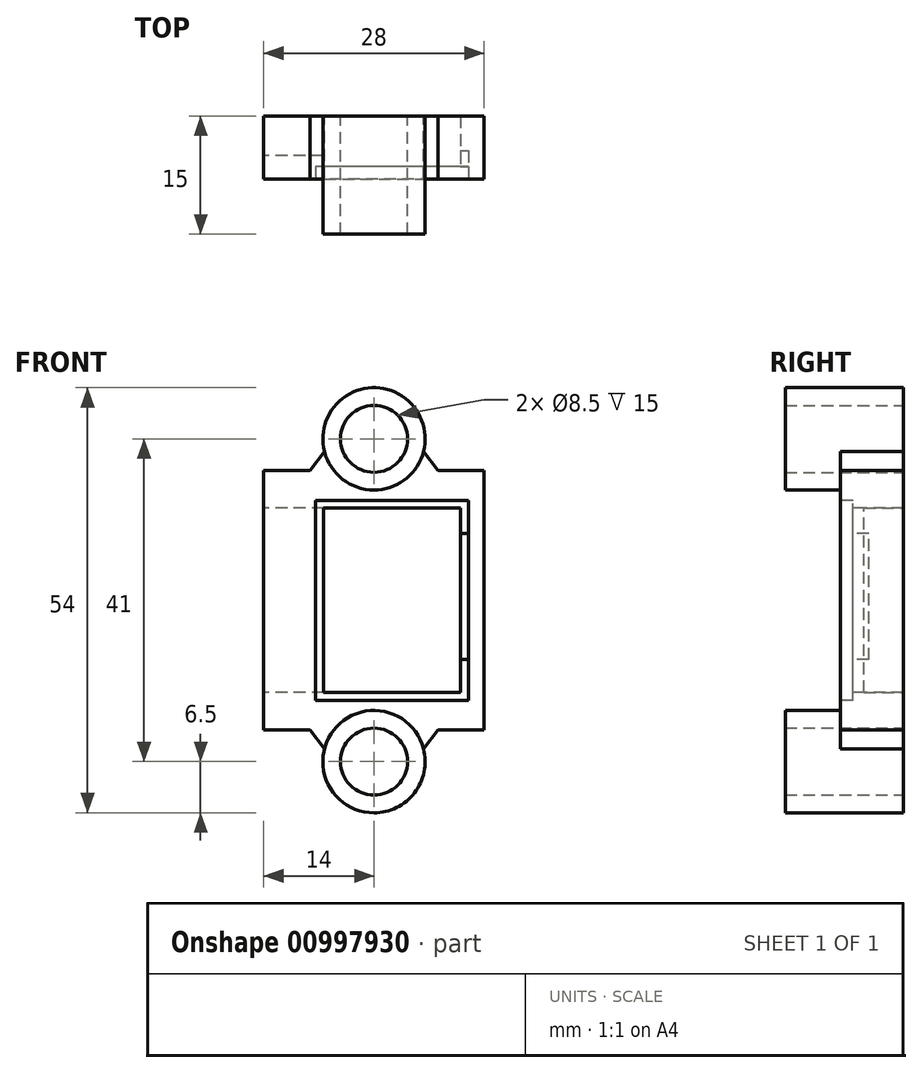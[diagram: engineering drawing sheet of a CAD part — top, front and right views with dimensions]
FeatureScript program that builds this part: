
annotation { "Feature Type Name" : "Feature", "Feature Type Description" : "" }
export const myFeature = defineFeature(function(context is Context, id is Id, definition is map)
    precondition{}
    {
        {
            var Q0;
            Q0=qCreatedBy(makeId("Front.planeOp"),FACE);
            var sketch = newSketch(context, id + "F0", { "sketchPlane" : qUnion([Q0])});
            skLineSegment(sketch, "E0.bottom", {"start": v(14, -16.5) * mm, "end": v(-14, -16.5) * mm});
            skLineSegment(sketch, "E0.top", {"start": v(14, 16.5) * mm, "end": v(-14, 16.5) * mm});
            skLineSegment(sketch, "E0.left", {"start": v(14, -16.5) * mm, "end": v(14, 16.5) * mm});
            skLineSegment(sketch, "E0.right", {"start": v(-14, -16.5) * mm, "end": v(-14, 16.5) * mm});
            skPoint(sketch, "E0.middle", {"position": v(0, 0) * mm});
            skCircle(sketch, "E1", {"center": v(0, 20.5) * mm, "radius": 6.5 * mm});
            skCircle(sketch, "E2", {"center": v(0, -20.5) * mm, "radius": 6.5 * mm});
            skCircle(sketch, "E3", {"center": v(0, 20.5) * mm, "radius": 4.25 * mm});
            skCircle(sketch, "E4", {"center": v(0, -20.5) * mm, "radius": 4.25 * mm});
            skSolve(sketch);
        }
        {
            var Q0;
            {var subQ7=sQuery(id+"F0.wireOp",EDGE,"E0.left");Q0=makeQuery(id+"F0.imprint","IMPRINT",FACE,{"disambiguationData":[TD([[makeQuery(id+"F0.imprint","IMPRINT",EDGE,{"derivedFrom":subQ7}),1.0]])]});}
            extrude(context, id + "F1", {"entities" : qUnion([Q0]), "depth" : 8 * mm, "offsetDistance" : 25 * mm});
        }
        {
            var Q0;
            {var subQ0=sQuery(id+"F0.wireOp",EDGE,"E1");var subQ1=sQuery(id+"F0.wireOp",EDGE,"E0.top");var subQ2=makeQuery(id+"F0.imprint","INTERSECT",VERTEX,{"disambiguationData":[OD(0.0)],"derivedFrom":[subQ1,subQ0]});Q0=makeQuery(id+"F0.imprint","IMPRINT",FACE,{"disambiguationData":[TD([[makeQuery(id+"F0.imprint","IMPRINT",EDGE,{"disambiguationData":[TD([[subQ2,-1.0]])],"derivedFrom":subQ1}),-1.0]])]});}
            var Q1;
            {var subQ0=sQuery(id+"F0.wireOp",EDGE,"E1");var subQ1=sQuery(id+"F0.wireOp",EDGE,"E0.top");var subQ2=makeQuery(id+"F0.imprint","INTERSECT",VERTEX,{"disambiguationData":[OD(0.0)],"derivedFrom":[subQ1,subQ0]});Q1=makeQuery(id+"F0.imprint","IMPRINT",FACE,{"disambiguationData":[TD([[makeQuery(id+"F0.imprint","IMPRINT",EDGE,{"disambiguationData":[TD([[subQ2,-1.0]])],"derivedFrom":subQ1}),1.0]])]});}
            var Q2;
            {var subQ0=sQuery(id+"F0.wireOp",EDGE,"E2");var subQ1=sQuery(id+"F0.wireOp",EDGE,"E0.bottom");var subQ2=makeQuery(id+"F0.imprint","INTERSECT",VERTEX,{"disambiguationData":[OD(0.0)],"derivedFrom":[subQ1,subQ0]});Q2=makeQuery(id+"F0.imprint","IMPRINT",FACE,{"disambiguationData":[TD([[makeQuery(id+"F0.imprint","IMPRINT",EDGE,{"disambiguationData":[TD([[subQ2,-1.0]])],"derivedFrom":subQ1}),-1.0]])]});}
            var Q3;
            {var subQ0=sQuery(id+"F0.wireOp",EDGE,"E2");var subQ1=sQuery(id+"F0.wireOp",EDGE,"E0.bottom");var subQ2=makeQuery(id+"F0.imprint","INTERSECT",VERTEX,{"disambiguationData":[OD(0.0)],"derivedFrom":[subQ1,subQ0]});Q3=makeQuery(id+"F0.imprint","IMPRINT",FACE,{"disambiguationData":[TD([[makeQuery(id+"F0.imprint","IMPRINT",EDGE,{"disambiguationData":[TD([[subQ2,-1.0]])],"derivedFrom":subQ1}),1.0]])]});}
            extrude(context, id + "F2", {"entities" : qUnion([Q0, Q1, Q2, Q3]), "depth" : 14 * mm, "offsetDistance" : 25 * mm});
        }
        {
            var Q0;
            {var subQ0=sQuery(id+"F0.wireOp",EDGE,"E2");var subQ1=sQuery(id+"F0.wireOp",EDGE,"E0.bottom");var subQ2=makeQuery(id+"F0.imprint","INTERSECT",VERTEX,{"disambiguationData":[OD(0.0)],"derivedFrom":[subQ1,subQ0]});Q0=makeQuery(id+"F0.imprint","IMPRINT",FACE,{"disambiguationData":[TD([[makeQuery(id+"F0.imprint","IMPRINT",EDGE,{"disambiguationData":[TD([[subQ2,-1.0]])],"derivedFrom":subQ1}),1.0]])]});}
            var Q1;
            {var subQ0=sQuery(id+"F0.wireOp",EDGE,"E2");var subQ1=sQuery(id+"F0.wireOp",EDGE,"E0.bottom");var subQ2=makeQuery(id+"F0.imprint","INTERSECT",VERTEX,{"disambiguationData":[OD(0.0)],"derivedFrom":[subQ1,subQ0]});Q1=makeQuery(id+"F0.imprint","IMPRINT",FACE,{"disambiguationData":[TD([[makeQuery(id+"F0.imprint","IMPRINT",EDGE,{"disambiguationData":[TD([[subQ2,-1.0]])],"derivedFrom":subQ1}),-1.0]])]});}
            var Q2;
            {var subQ0=sQuery(id+"F0.wireOp",EDGE,"E1");var subQ1=sQuery(id+"F0.wireOp",EDGE,"E0.top");var subQ2=makeQuery(id+"F0.imprint","INTERSECT",VERTEX,{"disambiguationData":[OD(0.0)],"derivedFrom":[subQ1,subQ0]});Q2=makeQuery(id+"F0.imprint","IMPRINT",FACE,{"disambiguationData":[TD([[makeQuery(id+"F0.imprint","IMPRINT",EDGE,{"disambiguationData":[TD([[subQ2,-1.0]])],"derivedFrom":subQ1}),1.0]])]});}
            var Q3;
            {var subQ0=sQuery(id+"F0.wireOp",EDGE,"E1");var subQ1=sQuery(id+"F0.wireOp",EDGE,"E0.top");var subQ2=makeQuery(id+"F0.imprint","INTERSECT",VERTEX,{"disambiguationData":[OD(0.0)],"derivedFrom":[subQ1,subQ0]});Q3=makeQuery(id+"F0.imprint","IMPRINT",FACE,{"disambiguationData":[TD([[makeQuery(id+"F0.imprint","IMPRINT",EDGE,{"disambiguationData":[TD([[subQ2,-1.0]])],"derivedFrom":subQ1}),-1.0]])]});}
            extrude(context, id + "F3", {"entities" : qUnion([Q0, Q1, Q2, Q3]), "operationType" : NewBodyOperationType.ADD, "depth" : 15 * mm, "offsetDistance" : 25 * mm});
        }
        {
            var Q0;
            {var subQ0=sQuery(id+"F0.wireOp",EDGE,"E1");var subQ1=sQuery(id+"F0.wireOp",EDGE,"E0.top");Q0=makeQuery(id+"F1.opExtrude","SWEPT_EDGE",EDGE,{"disambiguationData":[OSD([subQ1,subQ0]),TDD([makeQuery(id+"F0.imprint","INTERSECT",VERTEX,{"disambiguationData":[OD(1.0)],"derivedFrom":[subQ1,subQ0]})])]});}
            var Q1;
            {var subQ0=sQuery(id+"F0.wireOp",EDGE,"E1");var subQ1=sQuery(id+"F0.wireOp",EDGE,"E0.top");Q1=makeQuery(id+"F1.opExtrude","SWEPT_EDGE",EDGE,{"disambiguationData":[OSD([subQ1,subQ0]),TDD([makeQuery(id+"F0.imprint","INTERSECT",VERTEX,{"disambiguationData":[OD(0.0)],"derivedFrom":[subQ1,subQ0]})])]});}
            var Q2;
            {var subQ0=sQuery(id+"F0.wireOp",EDGE,"E2");var subQ1=sQuery(id+"F0.wireOp",EDGE,"E0.bottom");Q2=makeQuery(id+"F1.opExtrude","SWEPT_EDGE",EDGE,{"disambiguationData":[OSD([subQ1,subQ0]),TDD([makeQuery(id+"F0.imprint","INTERSECT",VERTEX,{"disambiguationData":[OD(0.0)],"derivedFrom":[subQ1,subQ0]})])]});}
            var Q3;
            {var subQ0=sQuery(id+"F0.wireOp",EDGE,"E2");var subQ1=sQuery(id+"F0.wireOp",EDGE,"E0.bottom");Q3=makeQuery(id+"F1.opExtrude","SWEPT_EDGE",EDGE,{"disambiguationData":[OSD([subQ1,subQ0]),TDD([makeQuery(id+"F0.imprint","INTERSECT",VERTEX,{"disambiguationData":[OD(1.0)],"derivedFrom":[subQ1,subQ0]})])]});}
            chamfer(context, id + "F4", {"entities" : qUnion([Q0, Q1, Q2, Q3]), "width" : 1.9 * mm, "tangentPropagation" : true});
        }
        {
            var Q0;
            Q0=makeQuery(id+"F1.opExtrude","CAP_FACE",FACE,{"disambiguationData":[OSD([sQuery(id+"F0.wireOp",EDGE,"E0.bottom"),sQuery(id+"F0.wireOp",EDGE,"E0.top"),sQuery(id+"F0.wireOp",EDGE,"E0.left"),sQuery(id+"F0.wireOp",EDGE,"E0.right"),sQuery(id+"F0.wireOp",EDGE,"E1"),sQuery(id+"F0.wireOp",EDGE,"E2")])],"isStart":false});
            var sketch = newSketch(context, id + "F5", { "sketchPlane" : qUnion([Q0])});
            skLineSegment(sketch, "E5.bottom", {"start": v(12, -12.7) * mm, "end": v(-7.4, -12.7) * mm});
            skLineSegment(sketch, "E5.top", {"start": v(12, 12.7) * mm, "end": v(-7.4, 12.7) * mm});
            skLineSegment(sketch, "E5.left", {"start": v(12, -12.7) * mm, "end": v(12, 12.7) * mm});
            skLineSegment(sketch, "E5.right", {"start": v(-7.4, -12.7) * mm, "end": v(-7.4, 12.7) * mm});
            skPoint(sketch, "E5.middle", {"position": v(2.3, 0) * mm});
            skSolve(sketch);
        }
        {
            var Q0;
            Q0 = qSketchRegion(id + "F5", true);
            extrude(context, id + "F6", {"entities" : qUnion([Q0]), "operationType" : NewBodyOperationType.REMOVE, "oppositeDirection" : true, "depth" : 1.6 * mm, "offsetDistance" : 25 * mm});
        }
        {
            var Q0;
            Q0=makeQuery(id+"F6.boolean.opBoolean","COPY",FACE,{"derivedFrom":makeQuery(id+"F6.opExtrude","CAP_FACE",FACE,{"disambiguationData":[OSD([sQuery(id+"F5.wireOp",EDGE,"E5.bottom"),sQuery(id+"F5.wireOp",EDGE,"E5.top"),sQuery(id+"F5.wireOp",EDGE,"E5.left"),sQuery(id+"F5.wireOp",EDGE,"E5.right")])],"isStart":false})});
            var sketch = newSketch(context, id + "F7", { "sketchPlane" : qUnion([Q0])});
            skLineSegment(sketch, "E6.bottom", {"start": v(11, -11.7) * mm, "end": v(-6.4, -11.7) * mm});
            skLineSegment(sketch, "E6.top", {"start": v(11, 11.7) * mm, "end": v(-6.4, 11.7) * mm});
            skLineSegment(sketch, "E6.left", {"start": v(11, -11.7) * mm, "end": v(11, 11.7) * mm});
            skLineSegment(sketch, "E6.right", {"start": v(-6.4, -11.7) * mm, "end": v(-6.4, 11.7) * mm});
            skPoint(sketch, "E6.middle", {"position": v(2.3, 0) * mm});
            skSolve(sketch);
        }
        {
            var Q0;
            Q0=makeQuery(id+"F7.imprint","IMPRINT",FACE,{"disambiguationData":[TD([[makeQuery(id+"F7.imprint","IMPRINT",EDGE,{"derivedFrom":sQuery(id+"F7.wireOp",EDGE,"E6.bottom")}),-1.0]])]});
            extrude(context, id + "F8", {"entities" : qUnion([Q0]), "operationType" : NewBodyOperationType.REMOVE, "oppositeDirection" : true, "depth" : 25 * mm, "offsetDistance" : 25 * mm});
        }
        {
            var Q0;
            {var subQ7=sQuery(id+"F0.wireOp",EDGE,"E0.left");Q0=makeQuery(id+"F0.imprint","IMPRINT",FACE,{"disambiguationData":[TD([[makeQuery(id+"F0.imprint","IMPRINT",EDGE,{"derivedFrom":subQ7}),1.0]])]});}
            var sketch = newSketch(context, id + "F9", { "sketchPlane" : qUnion([Q0])});
            skLineSegment(sketch, "E7.bottom", {"start": v(3.7, -11.7) * mm, "end": v(-16.31, -11.7) * mm});
            skLineSegment(sketch, "E7.top", {"start": v(3.7, 11.7) * mm, "end": v(-16.31, 11.7) * mm});
            skLineSegment(sketch, "E7.left", {"start": v(3.7, -11.7) * mm, "end": v(3.7, 11.7) * mm});
            skLineSegment(sketch, "E7.right", {"start": v(-16.31, -11.7) * mm, "end": v(-16.31, 11.7) * mm});
            skPoint(sketch, "E7.middle", {"position": v(-6.3, 0) * mm});
            skSolve(sketch);
        }
        {
            var Q0;
            {var subQ0=sQuery(id+"F9.wireOp",EDGE,"E7.left");Q0=makeQuery(id+"F9.imprint","IMPRINT",FACE,{"disambiguationData":[TD([[makeQuery(id+"F9.imprint","IMPRINT",EDGE,{"derivedFrom":subQ0}),1.0]])]});}
            extrude(context, id + "F10", {"entities" : qUnion([Q0]), "operationType" : NewBodyOperationType.REMOVE, "depth" : 5 * mm, "offsetDistance" : 25 * mm});
        }
        {
            var Q0;
            Q0=makeQuery(id+"F6.boolean.opBoolean","COPY",FACE,{"derivedFrom":makeQuery(id+"F6.opExtrude","CAP_FACE",FACE,{"disambiguationData":[OSD([sQuery(id+"F5.wireOp",EDGE,"E5.bottom"),sQuery(id+"F5.wireOp",EDGE,"E5.top"),sQuery(id+"F5.wireOp",EDGE,"E5.left"),sQuery(id+"F5.wireOp",EDGE,"E5.right")])],"isStart":false})});
            var sketch = newSketch(context, id + "F11", { "sketchPlane" : qUnion([Q0])});
            skLineSegment(sketch, "E8.bottom", {"start": v(10, -7.53) * mm, "end": v(12, -7.53) * mm});
            skLineSegment(sketch, "E8.top", {"start": v(10, 8.47) * mm, "end": v(12, 8.47) * mm});
            skLineSegment(sketch, "E8.left", {"start": v(10, -7.53) * mm, "end": v(10, 8.47) * mm});
            skLineSegment(sketch, "E8.right", {"start": v(12, -7.53) * mm, "end": v(12, 8.47) * mm});
            skPoint(sketch, "E8.middle", {"position": v(11, 0.47) * mm});
            skSolve(sketch);
        }
        {
            var Q0;
            {var subQ0=sQuery(id+"F11.wireOp",EDGE,"E8.right");Q0=makeQuery(id+"F11.imprint","IMPRINT",FACE,{"disambiguationData":[TD([[makeQuery(id+"F11.imprint","IMPRINT",EDGE,{"derivedFrom":subQ0}),1.0]])]});}
            extrude(context, id + "F12", {"entities" : qUnion([Q0]), "operationType" : NewBodyOperationType.REMOVE, "oppositeDirection" : true, "depth" : 2 * mm, "offsetDistance" : 25 * mm});
        }
    });
